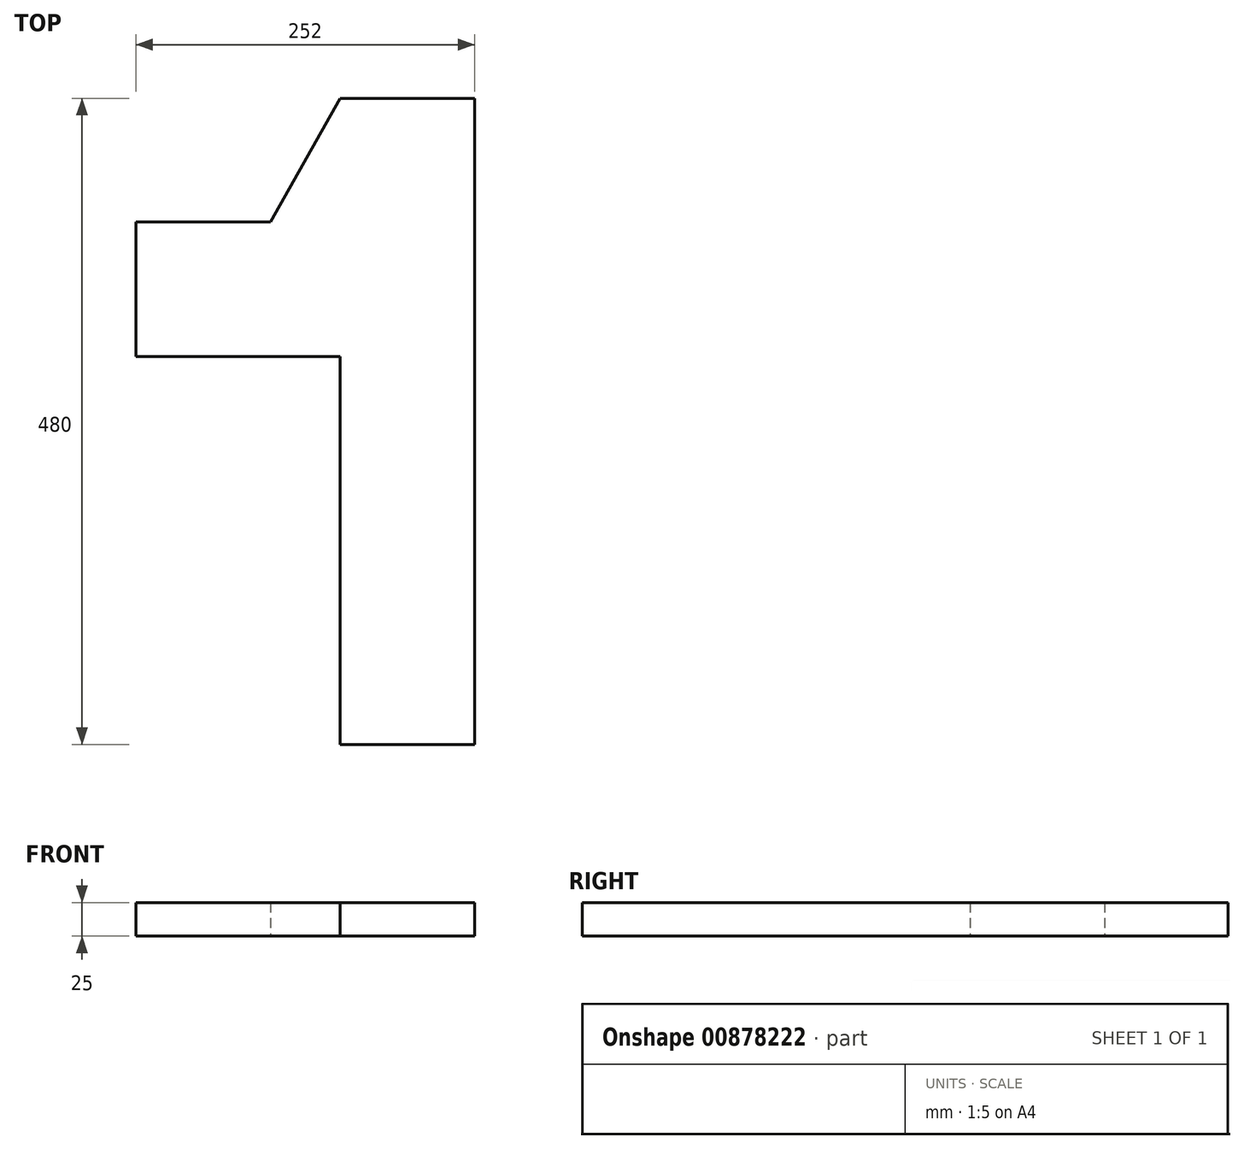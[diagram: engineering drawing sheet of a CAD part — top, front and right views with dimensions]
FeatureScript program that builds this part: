
annotation { "Feature Type Name" : "Feature", "Feature Type Description" : "" }
export const myFeature = defineFeature(function(context is Context, id is Id, definition is map)
    precondition{}
    {
        {
            var Q0;
            Q0=qCreatedBy(makeId("Top.planeOp"),FACE);
            var sketch = newSketch(context, id + "F0", { "sketchPlane" : qUnion([Q0])});
            skLineSegment(sketch, "E0", {"start": v(-228.34, 467.34) * mm, "end": v(-128.34, 467.34) * mm});
            skLineSegment(sketch, "E1", {"start": v(-128.34, 467.34) * mm, "end": v(-128.34, -12.66) * mm});
            skLineSegment(sketch, "E2", {"start": v(-128.34, -12.66) * mm, "end": v(-228.34, -12.66) * mm});
            skLineSegment(sketch, "E3", {"start": v(-228.34, -12.66) * mm, "end": v(-228.34, 275.41) * mm});
            skLineSegment(sketch, "E4", {"start": v(-228.34, 275.41) * mm, "end": v(-380.34, 275.41) * mm});
            skLineSegment(sketch, "E5", {"start": v(-380.34, 275.41) * mm, "end": v(-380.34, 375.41) * mm});
            skLineSegment(sketch, "E6", {"start": v(-380.34, 375.41) * mm, "end": v(-280.34, 375.41) * mm});
            skLineSegment(sketch, "E7", {"start": v(-228.34, 467.34) * mm, "end": v(-280.34, 375.41) * mm});
            skSolve(sketch);
        }
        {
            var Q0;
            Q0 = qSketchRegion(id + "F0", true);
            extrude(context, id + "F1", {"entities" : qUnion([Q0]), "depth" : 25 * mm, "offsetDistance" : 25 * mm});
        }
        {
            var Q0;
            Q0 = qSketchRegion(id + "F0", true);
            extrude(context, id + "F2", {"entities" : qUnion([Q0]), "operationType" : NewBodyOperationType.ADD, "depth" : 25 * mm, "offsetDistance" : 25 * mm});
        }
        {
            var Q0;
            Q0 = qSketchRegion(id + "F0", true);
            extrude(context, id + "F3", {"entities" : qUnion([Q0]), "operationType" : NewBodyOperationType.ADD, "depth" : 25 * mm, "offsetDistance" : 25 * mm});
        }
        {
            var Q0;
            Q0 = qSketchRegion(id + "F0", true);
            extrude(context, id + "F4", {"entities" : qUnion([Q0]), "operationType" : NewBodyOperationType.ADD, "depth" : 25 * mm, "offsetDistance" : 25 * mm});
        }
    });
